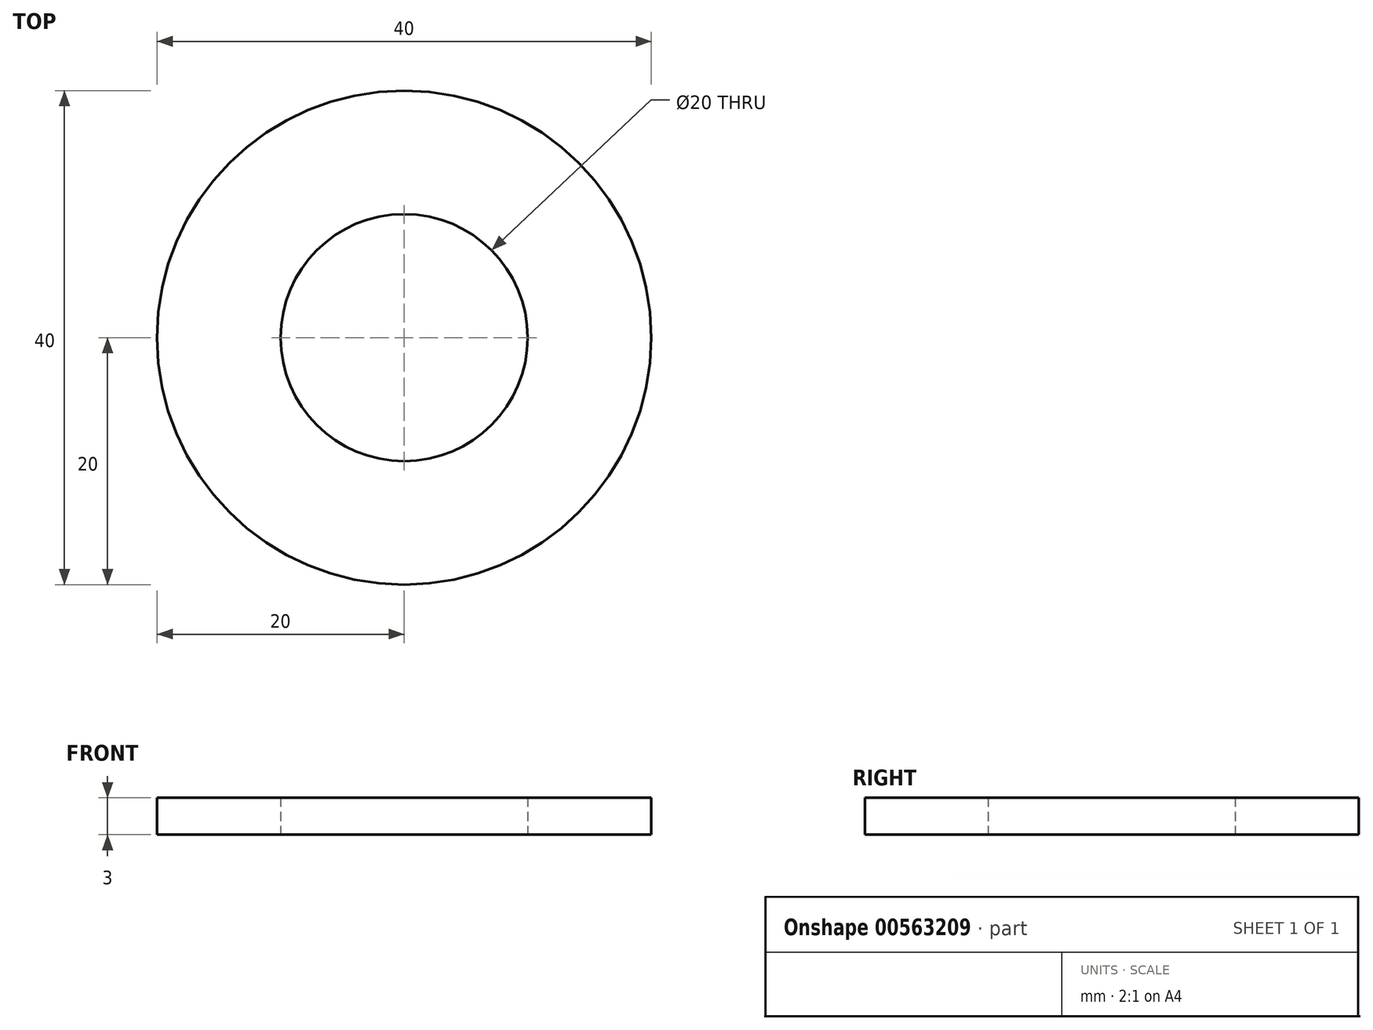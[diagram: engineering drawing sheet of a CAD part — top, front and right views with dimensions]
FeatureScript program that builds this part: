
annotation { "Feature Type Name" : "Feature", "Feature Type Description" : "" }
export const myFeature = defineFeature(function(context is Context, id is Id, definition is map)
    precondition{}
    {
        {
            var Q0;
            Q0=qCreatedBy(makeId("Top.planeOp"),FACE);
            var sketch = newSketch(context, id + "F0", { "sketchPlane" : qUnion([Q0])});
            skCircle(sketch, "E0", {"center": v(0, 0) * mm, "radius": 20 * mm});
            skCircle(sketch, "E1", {"center": v(0, 0) * mm, "radius": 10 * mm});
            skSolve(sketch);
        }
        {
            var Q0;
            Q0 = qSketchRegion(id + "F0", true);
            extrude(context, id + "F1", {"entities" : qUnion([Q0]), "endBound" : BoundingType.SYMMETRIC, "depth" : 3 * mm, "offsetDistance" : 25 * mm});
        }
    });
